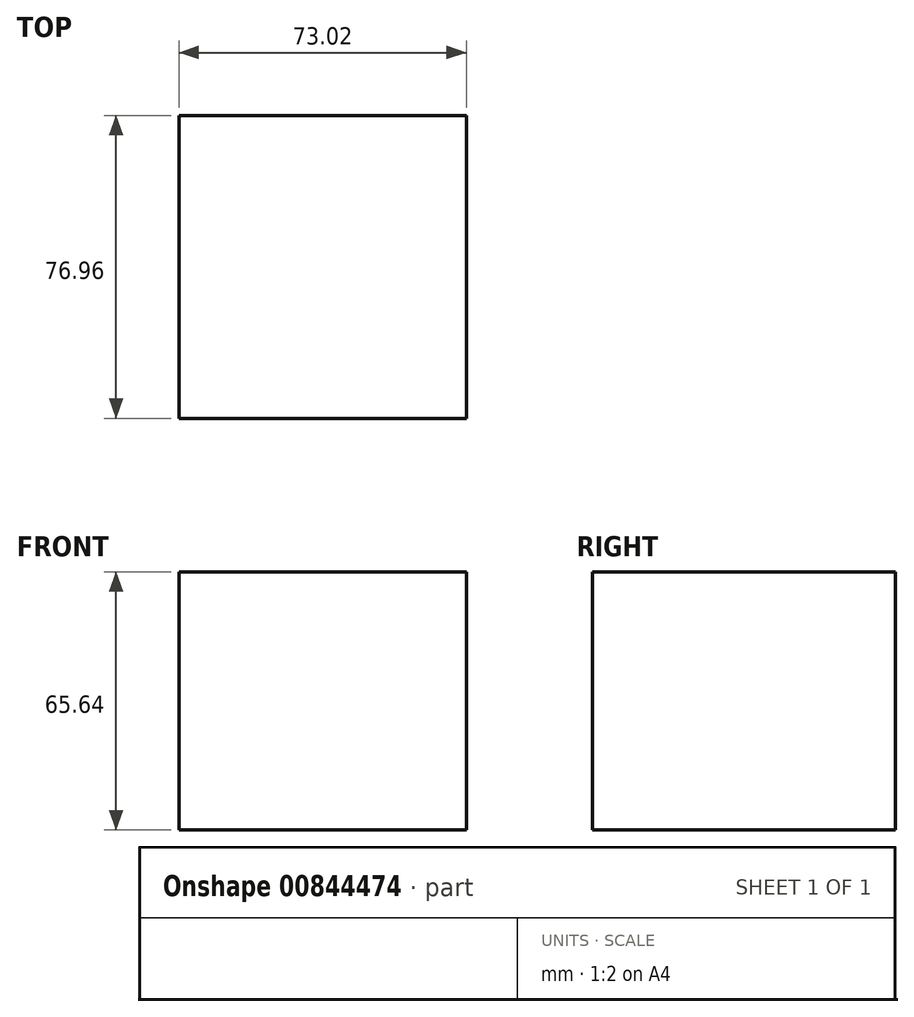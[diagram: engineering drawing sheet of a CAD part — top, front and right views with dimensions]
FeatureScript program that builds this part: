
annotation { "Feature Type Name" : "Feature", "Feature Type Description" : "" }
export const myFeature = defineFeature(function(context is Context, id is Id, definition is map)
    precondition{}
    {
        {
            var Q0;
            Q0=qCreatedBy(makeId("Front.planeOp"),FACE);
            var sketch = newSketch(context, id + "F0", { "sketchPlane" : qUnion([Q0])});
            skLineSegment(sketch, "E0.bottom", {"start": v(-36.5, 32.82) * mm, "end": v(36.5, 32.82) * mm});
            skLineSegment(sketch, "E0.top", {"start": v(-36.5, -32.82) * mm, "end": v(36.5, -32.82) * mm});
            skLineSegment(sketch, "E0.left", {"start": v(-36.5, 32.82) * mm, "end": v(-36.5, -32.82) * mm});
            skLineSegment(sketch, "E0.right", {"start": v(36.5, 32.82) * mm, "end": v(36.5, -32.82) * mm});
            skPoint(sketch, "E0.middle", {"position": v(0, 0) * mm});
            skSolve(sketch);
        }
        {
            var Q0;
            Q0=makeQuery(id+"F0.imprint","IMPRINT",FACE,{"disambiguationData":[TD([[makeQuery(id+"F0.imprint","IMPRINT",EDGE,{"derivedFrom":sQuery(id+"F0.wireOp",EDGE,"E0.bottom")}),-1.0]])]});
            extrude(context, id + "F1", {"entities" : qUnion([Q0]), "depth" : 76.96 * mm, "offsetDistance" : 25.4 * mm});
        }
    });
